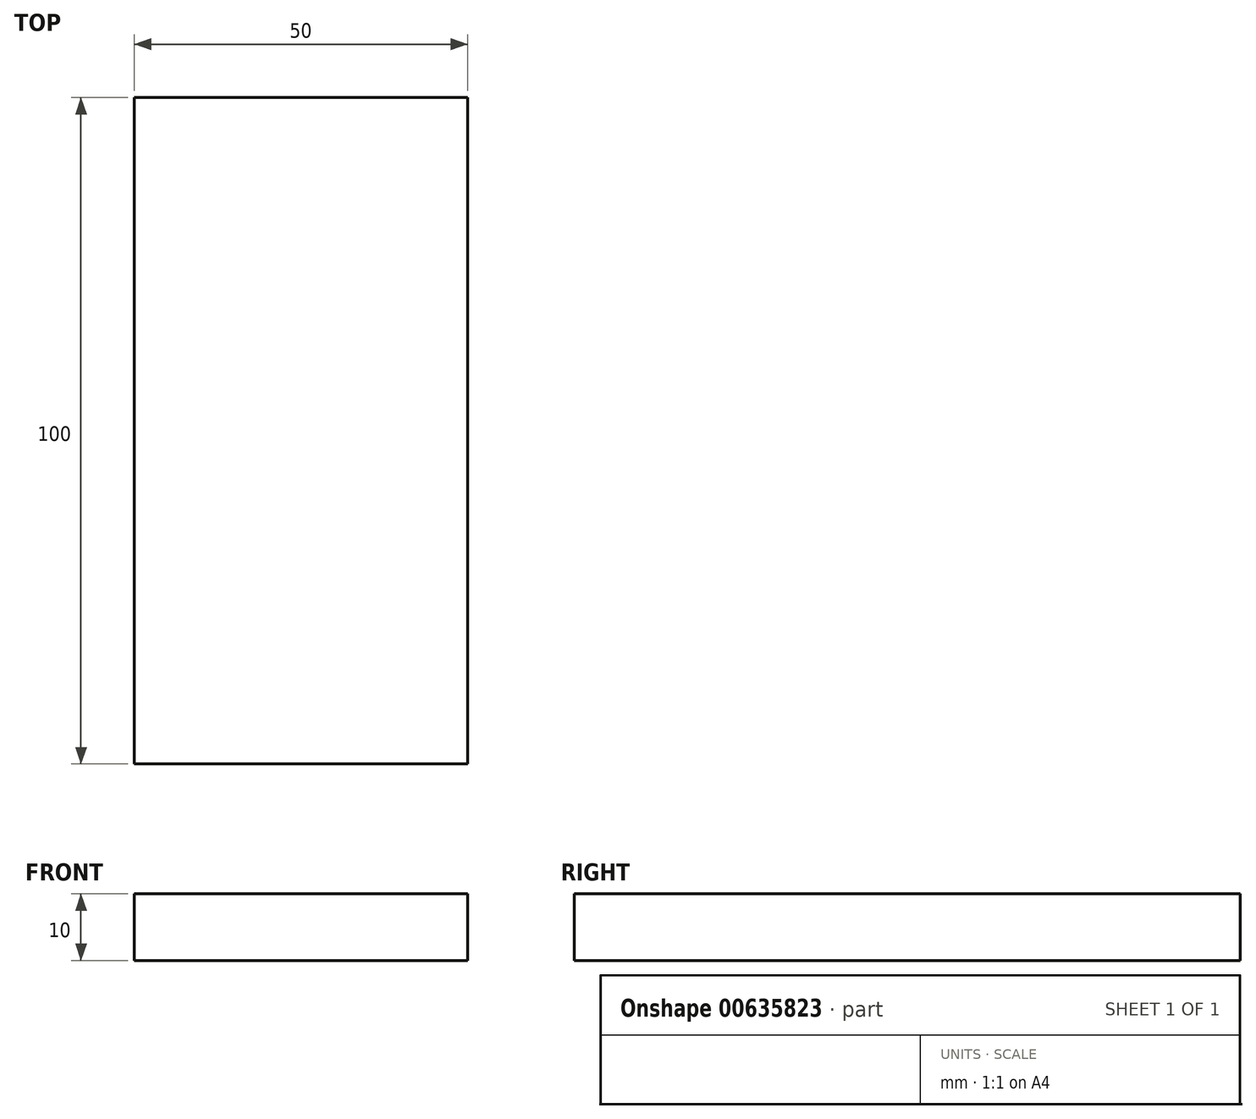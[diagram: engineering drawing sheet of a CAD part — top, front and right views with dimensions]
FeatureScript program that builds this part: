
annotation { "Feature Type Name" : "Feature", "Feature Type Description" : "" }
export const myFeature = defineFeature(function(context is Context, id is Id, definition is map)
    precondition{}
    {
        {
            var Q0;
            Q0=qCreatedBy(makeId("Top.planeOp"),FACE);
            var sketch = newSketch(context, id + "F0", { "sketchPlane" : qUnion([Q0])});
            skLineSegment(sketch, "E0.bottom", {"start": v(-25, 50) * mm, "end": v(25, 50) * mm});
            skLineSegment(sketch, "E0.top", {"start": v(-25, -50) * mm, "end": v(25, -50) * mm});
            skLineSegment(sketch, "E0.left", {"start": v(-25, 50) * mm, "end": v(-25, -50) * mm});
            skLineSegment(sketch, "E0.right", {"start": v(25, 50) * mm, "end": v(25, -50) * mm});
            skPoint(sketch, "E0.middle", {"position": v(0, 0) * mm});
            skSolve(sketch);
        }
        {
            var Q0;
            Q0=makeQuery(id+"F0.imprint","IMPRINT",FACE,{"disambiguationData":[TD([[makeQuery(id+"F0.imprint","IMPRINT",EDGE,{"derivedFrom":sQuery(id+"F0.wireOp",EDGE,"E0.bottom")}),-1.0]])]});
            extrude(context, id + "F1", {"entities" : qUnion([Q0]), "depth" : 10 * mm, "offsetDistance" : 25 * mm});
        }
    });
